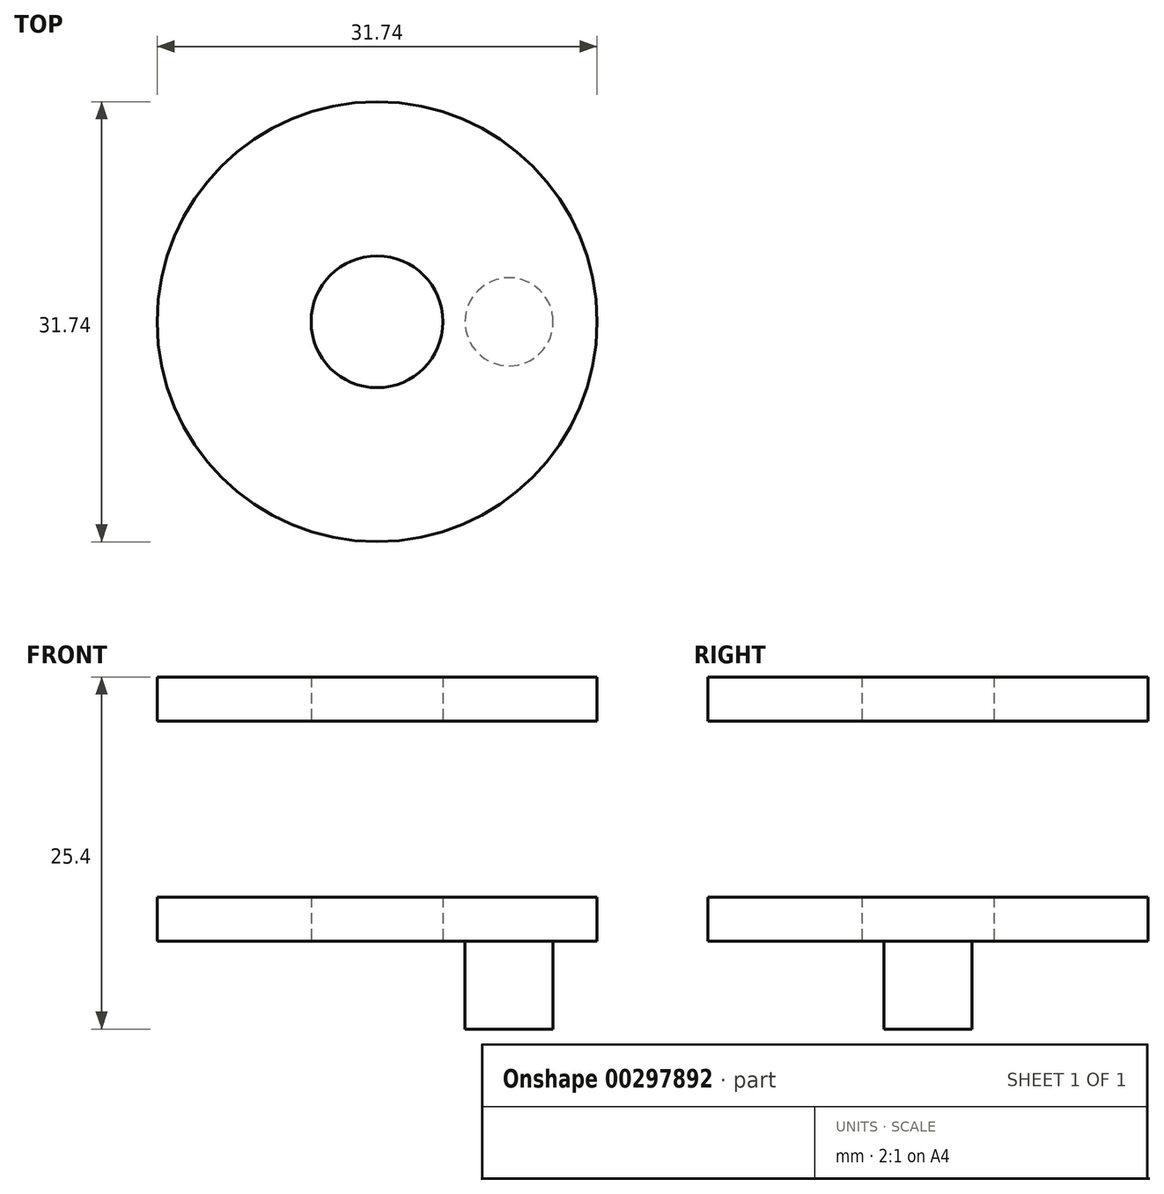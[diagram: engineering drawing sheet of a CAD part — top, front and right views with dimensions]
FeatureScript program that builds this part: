
annotation { "Feature Type Name" : "Feature", "Feature Type Description" : "" }
export const myFeature = defineFeature(function(context is Context, id is Id, definition is map)
    precondition{}
    {
        {
            var Q0;
            Q0=qCreatedBy(makeId("Front.planeOp"),FACE);
            var sketch = newSketch(context, id + "F0", { "sketchPlane" : qUnion([Q0])});
            skLineSegment(sketch, "E0.bottom", {"start": v(0, -4.74) * mm, "end": v(4.76, -4.74) * mm});
            skLineSegment(sketch, "E0.top", {"start": v(0, 14.3) * mm, "end": v(4.76, 14.3) * mm});
            skLineSegment(sketch, "E0.left", {"start": v(0, -4.74) * mm, "end": v(0, 14.3) * mm});
            skLineSegment(sketch, "E0.right", {"start": v(4.76, -4.74) * mm, "end": v(4.76, 14.3) * mm});
            skLineSegment(sketch, "E1.bottom", {"start": v(4.76, 14.3) * mm, "end": v(15.87, 14.3) * mm});
            skLineSegment(sketch, "E1.top", {"start": v(4.76, 11.13) * mm, "end": v(15.87, 11.13) * mm});
            skLineSegment(sketch, "E1.left", {"start": v(4.76, 14.3) * mm, "end": v(4.76, 11.13) * mm});
            skLineSegment(sketch, "E1.right", {"start": v(15.87, 14.3) * mm, "end": v(15.87, 11.13) * mm});
            skLineSegment(sketch, "E2.bottom", {"start": v(4.76, -4.74) * mm, "end": v(15.87, -4.74) * mm});
            skLineSegment(sketch, "E2.top", {"start": v(4.76, -1.57) * mm, "end": v(15.87, -1.57) * mm});
            skLineSegment(sketch, "E2.left", {"start": v(4.76, -4.74) * mm, "end": v(4.76, -1.57) * mm});
            skLineSegment(sketch, "E2.right", {"start": v(15.87, -4.74) * mm, "end": v(15.87, -1.57) * mm});
            skLineSegment(sketch, "E3.bottom", {"start": v(4.76, 11.13) * mm, "end": v(12.7, 11.13) * mm});
            skLineSegment(sketch, "E3.top", {"start": v(4.76, -1.57) * mm, "end": v(12.7, -1.57) * mm});
            skLineSegment(sketch, "E3.left", {"start": v(4.76, 11.13) * mm, "end": v(4.76, -1.57) * mm});
            skLineSegment(sketch, "E3.right", {"start": v(12.7, 11.13) * mm, "end": v(12.7, -1.57) * mm});
            skSolve(sketch);
        }
        {
            var Q0;
            Q0=makeQuery(id+"F0.imprint","IMPRINT",FACE,{"disambiguationData":[TD([[makeQuery(id+"F0.imprint","IMPRINT",EDGE,{"derivedFrom":sQuery(id+"F0.wireOp",EDGE,"E1.bottom")}),-1.0]])]});
            var Q1;
            Q1=makeQuery(id+"F0.imprint","IMPRINT",FACE,{"disambiguationData":[TD([[makeQuery(id+"F0.imprint","IMPRINT",EDGE,{"derivedFrom":sQuery(id+"F0.wireOp",EDGE,"E3.bottom")}),-1.0]])]});
            var Q2;
            Q2=makeQuery(id+"F0.imprint","IMPRINT",FACE,{"disambiguationData":[TD([[makeQuery(id+"F0.imprint","IMPRINT",EDGE,{"derivedFrom":sQuery(id+"F0.wireOp",EDGE,"E2.bottom")}),1.0]])]});
            var Q3;
            Q3=sQuery(id+"F0.wireOp",EDGE,"E0.left");
            revolve(context, id + "F1", {"entities" : qUnion([Q0, Q1, Q2]), "axis" : qUnion([Q3]), "revolveType" : RevolveType.FULL});
        }
        {
            var Q0;
            Q0=makeQuery(id+"F1.opRevolve","SWEPT_FACE",FACE,{"disambiguationData":[OSD([sQuery(id+"F0.wireOp",EDGE,"E2.bottom")])]});
            var sketch = newSketch(context, id + "F2", { "sketchPlane" : qUnion([Q0])});
            skCircle(sketch, "E4", {"center": v(9.53, 0) * mm, "radius": 3.18 * mm});
            skSolve(sketch);
        }
        {
            var Q0;
            Q0=makeQuery(id+"F2.imprint","IMPRINT",FACE,{"disambiguationData":[TD([[makeQuery(id+"F2.imprint","IMPRINT",EDGE,{"derivedFrom":sQuery(id+"F2.wireOp",EDGE,"E4")}),1.0]])]});
            extrude(context, id + "F3", {"entities" : qUnion([Q0]), "operationType" : NewBodyOperationType.ADD, "depth" : 6.35 * mm});
        }
    });
